annotation { "Feature Type Name" : "Feature", "Feature Type Description" : "" }
export const myFeature = defineFeature(function(context is Context, id is Id, definition is map)
    precondition{}
    {
        {
            var Q0;
            Q0=qCreatedBy(makeId("Top.planeOp"),FACE);
            var sketch = newSketch(context, id + "F0", { "sketchPlane" : qUnion([Q0])});
            skArc(sketch, "E0", {"start": v(-21.17, 59.98) * mm, "mid": v(0, -63.6) * mm, "end": v(21.17, 59.98) * mm});
            skArc(sketch, "E1", {"start": v(21.17, 59.98) * mm, "mid": v(0, 85.08) * mm, "end": v(-21.17, 59.98) * mm});
            skArc(sketch, "E2", {"start": v(13.2, 62.22) * mm, "mid": v(0, 76.88) * mm, "end": v(-13.2, 62.22) * mm});
            skArc(sketch, "E3.trimOffspring", {"start": v(13.2, 62.22) * mm, "mid": v(0, 63.6) * mm, "end": v(-13.2, 62.22) * mm});
            skSolve(sketch);
        }
        {
            var Q0;
            Q0=makeQuery(id+"F0.imprint","IMPRINT",FACE,{"disambiguationData":[TD([[makeQuery(id+"F0.imprint","IMPRINT",EDGE,{"derivedFrom":sQuery(id+"F0.wireOp",EDGE,"E0")}),1.0]])]});
            extrude(context, id + "F1", {"entities" : qUnion([Q0]), "depth" : 11.94 * mm, "offsetDistance" : 25.4 * mm});
        }
        {
            var Q0;
            Q0=makeQuery(id+"F1.opExtrude","CAP_FACE",FACE,{"disambiguationData":[OSD([sQuery(id+"F0.wireOp",EDGE,"E0"),sQuery(id+"F0.wireOp",EDGE,"E1"),sQuery(id+"F0.wireOp",EDGE,"E2"),sQuery(id+"F0.wireOp",EDGE,"E3.trimOffspring")])],"isStart":false});
            var sketch = newSketch(context, id + "F2", { "sketchPlane" : qUnion([Q0])});
            skCircle(sketch, "E4", {"center": v(0, 0) * mm, "radius": 57.03 * mm});
            skSolve(sketch);
        }
        {
            var Q0;
            Q0=makeQuery(id+"F2.imprint","IMPRINT",FACE,{"disambiguationData":[TD([[makeQuery(id+"F2.imprint","IMPRINT",EDGE,{"derivedFrom":sQuery(id+"F2.wireOp",EDGE,"E4")}),1.0]])]});
            extrude(context, id + "F3", {"entities" : qUnion([Q0]), "operationType" : NewBodyOperationType.REMOVE, "oppositeDirection" : true, "depth" : 6.35 * mm, "offsetDistance" : 25.4 * mm});
        }
        {
            var Q0;
            Q0=makeQuery(id+"F3.boolean.opBoolean","COPY",FACE,{"derivedFrom":makeQuery(id+"F3.opExtrude","CAP_FACE",FACE,{"disambiguationData":[OSD([sQuery(id+"F2.wireOp",EDGE,"E4")])],"isStart":false})});
            var sketch = newSketch(context, id + "F4", { "sketchPlane" : qUnion([Q0])});
            skArc(sketch, "E5", {"start": v(-6.86, 47.44) * mm, "mid": v(-33.23, 39.3) * mm, "end": v(-48.06, 16.03) * mm});
            skArc(sketch, "E6", {"start": v(49.1, 16.65) * mm, "mid": v(30.72, 38.2) * mm, "end": v(3.95, 47.44) * mm});
            skArc(sketch, "E7", {"start": v(14.15, -48.05) * mm, "mid": v(39.84, -26.07) * mm, "end": v(49.1, 6.46) * mm});
            skArc(sketch, "E8", {"start": v(-48.06, 4.8) * mm, "mid": v(-35.9, -31) * mm, "end": v(-3.54, -50.55) * mm});
            skArc(sketch, "E9", {"start": v(-48.06, 16.03) * mm, "mid": v(-27.06, 14.65) * mm, "end": v(-6.03, 14.15) * mm});
            skArc(sketch, "E10", {"start": v(-6.86, 47.44) * mm, "mid": v(-6.51, 30.8) * mm, "end": v(-6.03, 14.15) * mm});
            skArc(sketch, "E11", {"start": v(3.95, 47.44) * mm, "mid": v(2.87, 30.81) * mm, "end": v(3.11, 14.15) * mm});
            skArc(sketch, "E12", {"start": v(3.11, 14.15) * mm, "mid": v(26.14, 14.78) * mm, "end": v(49.1, 16.65) * mm});
            skArc(sketch, "E13", {"start": v(-48.06, 4.8) * mm, "mid": v(-27.04, 5.02) * mm, "end": v(-6.03, 5.54) * mm});
            skArc(sketch, "E14", {"start": v(-3.54, -50.55) * mm, "mid": v(-4.52, -22.5) * mm, "end": v(-6.03, 5.54) * mm});
            skArc(sketch, "E15", {"start": v(3.11, 4.8) * mm, "mid": v(6.67, -22.04) * mm, "end": v(14.15, -48.05) * mm});
            skArc(sketch, "E16", {"start": v(3.11, 4.8) * mm, "mid": v(26.11, 5.46) * mm, "end": v(49.1, 6.46) * mm});
            skCircle(sketch, "E17", {"center": v(-12.9, 20.74) * mm, "radius": 1.98 * mm});
            skCircle(sketch, "E18", {"center": v(-12.04, -0.6) * mm, "radius": 1.98 * mm});
            skCircle(sketch, "E19", {"center": v(10.77, -0.6) * mm, "radius": 1.98 * mm});
            skCircle(sketch, "E20", {"center": v(9.47, 20.74) * mm, "radius": 1.98 * mm});
            skSolve(sketch);
        }
        {
            var Q0;
            Q0=makeQuery(id+"F4.imprint","IMPRINT",FACE,{"disambiguationData":[TD([[makeQuery(id+"F4.imprint","IMPRINT",EDGE,{"derivedFrom":sQuery(id+"F4.wireOp",EDGE,"E5")}),1.0]])]});
            var Q1;
            Q1=makeQuery(id+"F4.imprint","IMPRINT",FACE,{"disambiguationData":[TD([[makeQuery(id+"F4.imprint","IMPRINT",EDGE,{"derivedFrom":sQuery(id+"F4.wireOp",EDGE,"E6")}),1.0]])]});
            var Q2;
            Q2=makeQuery(id+"F4.imprint","IMPRINT",FACE,{"disambiguationData":[TD([[makeQuery(id+"F4.imprint","IMPRINT",EDGE,{"derivedFrom":sQuery(id+"F4.wireOp",EDGE,"E8")}),1.0]])]});
            var Q3;
            Q3=makeQuery(id+"F4.imprint","IMPRINT",FACE,{"disambiguationData":[TD([[makeQuery(id+"F4.imprint","IMPRINT",EDGE,{"derivedFrom":sQuery(id+"F4.wireOp",EDGE,"E7")}),1.0]])]});
            extrude(context, id + "F5", {"entities" : qUnion([Q0, Q1, Q2, Q3]), "operationType" : NewBodyOperationType.ADD, "depth" : 2.54 * mm, "offsetDistance" : 25.4 * mm});
        }
        {
            var Q0;
            {var subQ0=sQuery(id+"F2.wireOp",EDGE,"E4");Q0=makeQuery(id+"F5.boolean.opBoolean","SPLIT",FACE,{"disambiguationData":[TD([makeQuery(id+"F3.boolean.opBoolean","COPY",FACE,{"derivedFrom":makeQuery(id+"F3.opExtrude","SWEPT_FACE",FACE,{"disambiguationData":[OSD([subQ0])]})})])],"derivedFrom":makeQuery(id+"F3.boolean.opBoolean","COPY",FACE,{"derivedFrom":makeQuery(id+"F3.opExtrude","CAP_FACE",FACE,{"disambiguationData":[OSD([subQ0])],"isStart":false})})});}
            var sketch = newSketch(context, id + "F6", { "sketchPlane" : qUnion([Q0])});
            skLineSegment(sketch, "E21.bottom", {"start": v(-19.07, 43.64) * mm, "end": v(-4.4, 43.64) * mm});
            skLineSegment(sketch, "E21.top", {"start": v(-10.85, 19.28) * mm, "end": v(-4.4, 19.28) * mm});
            skLineSegment(sketch, "E21.left", {"start": v(-10.85, 37.86) * mm, "end": v(-10.85, 19.28) * mm});
            skLineSegment(sketch, "E21.right", {"start": v(-4.4, 43.64) * mm, "end": v(-4.4, 19.28) * mm});
            skLineSegment(sketch, "E22", {"start": v(-19.07, 43.64) * mm, "end": v(-19.07, 37.86) * mm});
            skLineSegment(sketch, "E23", {"start": v(-19.07, 37.86) * mm, "end": v(-10.85, 37.86) * mm});
            skLineSegment(sketch, "E24.MirrorCS", {"start": v(4.4, 43.64) * mm, "end": v(4.4, 19.28) * mm});
            skLineSegment(sketch, "E25.MirrorCS", {"start": v(10.85, 19.28) * mm, "end": v(4.4, 19.28) * mm});
            skLineSegment(sketch, "E26.MirrorCS", {"start": v(10.85, 37.86) * mm, "end": v(10.85, 25.08) * mm});
            skLineSegment(sketch, "E27.MirrorCS", {"start": v(10.85, 43.64) * mm, "end": v(4.4, 43.64) * mm});
            skLineSegment(sketch, "E28", {"start": v(10.85, 19.28) * mm, "end": v(19.07, 19.28) * mm});
            skLineSegment(sketch, "E29", {"start": v(19.07, 19.28) * mm, "end": v(19.07, 25.08) * mm});
            skLineSegment(sketch, "E30", {"start": v(19.07, 25.08) * mm, "end": v(10.85, 25.08) * mm});
            skLineSegment(sketch, "E31", {"start": v(10.85, 37.86) * mm, "end": v(10.85, 43.64) * mm});
            skPoint(sketch, "E32.MirrorCS.end.orphan", {"position": v(19.07, 37.86) * mm});
            skPoint(sketch, "E32.MirrorCS.start.orphan", {"position": v(19.07, 43.64) * mm});
            skText(sketch, "E33", { "text": "Got Talent", "fontName": "RobotoSlab-Bold.ttf"});
            skText(sketch, "E34", { "text": "2017", "fontName": "RobotoSlab-Bold.ttf"});
            skText(sketch, "E35", { "text": "Best Overall", "fontName": "OpenSans-Bold.ttf"});
            skText(sketch, "E36", { "text": "Performance", "fontName": "OpenSans-Bold.ttf"});
            const initialGuessF6  = {"E33": [-0.04806, 0.00194, 1, 0, 0.01409], "E34": [-0.0157, -0.0105, 1, 0, 0.0105], "E35": [-0.03094, -0.02543, 1, 0, 0.00735], "E36": [-0.03096, -0.03522, 1, 0, 0.00682]};
            skSetInitialGuess(sketch, initialGuessF6);
            skSolve(sketch);
        }
        {
            var Q0;
            Q0 = qSketchRegion(id + "F6", true);
            extrude(context, id + "F7", {"entities" : qUnion([Q0]), "operationType" : NewBodyOperationType.ADD, "depth" : 6.35 * mm, "offsetDistance" : 25.4 * mm});
        }
    });